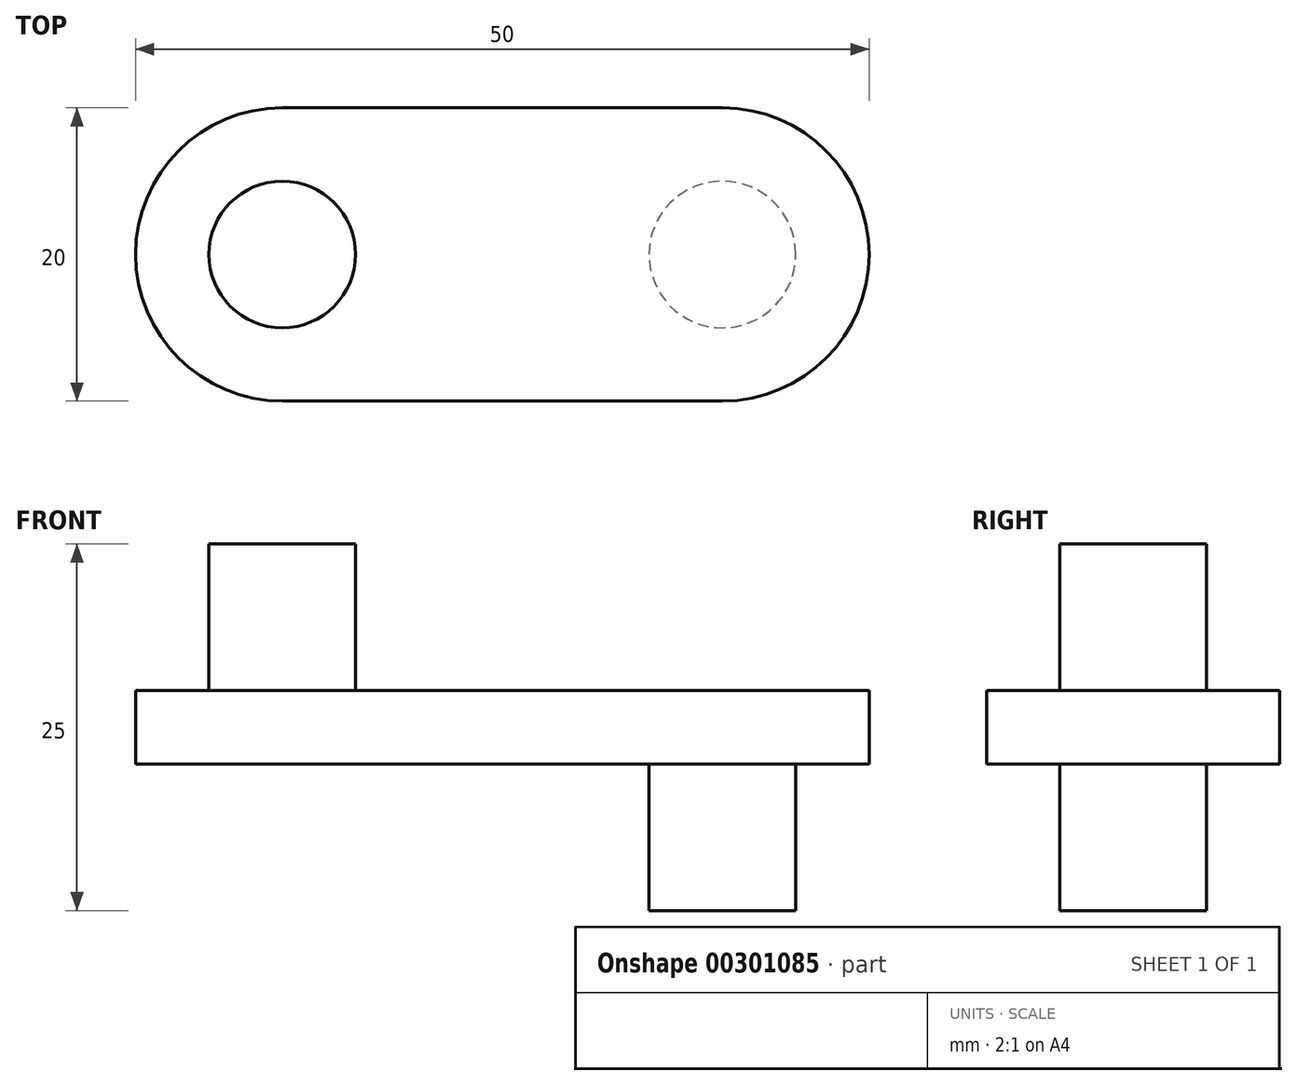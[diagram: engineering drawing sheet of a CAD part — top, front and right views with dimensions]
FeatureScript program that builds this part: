
annotation { "Feature Type Name" : "Feature", "Feature Type Description" : "" }
export const myFeature = defineFeature(function(context is Context, id is Id, definition is map)
    precondition{}
    {
        {
            var Q0;
            Q0=qCreatedBy(makeId("Top.planeOp"),FACE);
            var sketch = newSketch(context, id + "F0", { "sketchPlane" : qUnion([Q0])});
            skArc(sketch, "E0", {"start": v(0, 10) * mm, "mid": v(-10, 0) * mm, "end": v(0, -10) * mm});
            skArc(sketch, "E1", {"start": v(30, -10) * mm, "mid": v(40, 0) * mm, "end": v(30, 10) * mm});
            skLineSegment(sketch, "E2", {"start": v(0, 10) * mm, "end": v(30, 10) * mm});
            skLineSegment(sketch, "E3", {"start": v(0, -10) * mm, "end": v(30, -10) * mm});
            skSolve(sketch);
        }
        {
            var Q0;
            Q0=makeQuery(id+"F0.imprint","IMPRINT",FACE,{"disambiguationData":[TD([[makeQuery(id+"F0.imprint","IMPRINT",EDGE,{"derivedFrom":sQuery(id+"F0.wireOp",EDGE,"E0")}),1.0]])]});
            extrude(context, id + "F1", {"entities" : qUnion([Q0]), "depth" : 5 * mm});
        }
        {
            var Q0;
            Q0=makeQuery(id+"F1.opExtrude","CAP_FACE",FACE,{"disambiguationData":[OSD([sQuery(id+"F0.wireOp",EDGE,"E0"),sQuery(id+"F0.wireOp",EDGE,"E1"),sQuery(id+"F0.wireOp",EDGE,"E2"),sQuery(id+"F0.wireOp",EDGE,"E3")])],"isStart":false});
            var sketch = newSketch(context, id + "F2", { "sketchPlane" : qUnion([Q0])});
            skCircle(sketch, "E4", {"center": v(0, 0) * mm, "radius": 5 * mm});
            skSolve(sketch);
        }
        {
            var Q0;
            Q0=makeQuery(id+"F2.imprint","IMPRINT",FACE,{"disambiguationData":[TD([[makeQuery(id+"F2.imprint","IMPRINT",EDGE,{"derivedFrom":sQuery(id+"F2.wireOp",EDGE,"E4")}),1.0]])]});
            extrude(context, id + "F3", {"entities" : qUnion([Q0]), "operationType" : NewBodyOperationType.ADD, "depth" : 10 * mm});
        }
        {
            var Q0;
            Q0=makeQuery(id+"F1.opExtrude","CAP_FACE",FACE,{"disambiguationData":[OSD([sQuery(id+"F0.wireOp",EDGE,"E0"),sQuery(id+"F0.wireOp",EDGE,"E1"),sQuery(id+"F0.wireOp",EDGE,"E2"),sQuery(id+"F0.wireOp",EDGE,"E3")])],"isStart":true});
            var sketch = newSketch(context, id + "F4", { "sketchPlane" : qUnion([Q0])});
            skCircle(sketch, "E5", {"center": v(30, 0) * mm, "radius": 5 * mm});
            skSolve(sketch);
        }
        {
            var Q0;
            Q0=makeQuery(id+"F4.imprint","IMPRINT",FACE,{"disambiguationData":[TD([[makeQuery(id+"F4.imprint","IMPRINT",EDGE,{"derivedFrom":sQuery(id+"F4.wireOp",EDGE,"E5")}),1.0]])]});
            extrude(context, id + "F5", {"entities" : qUnion([Q0]), "operationType" : NewBodyOperationType.ADD, "depth" : 10 * mm});
        }
    });
